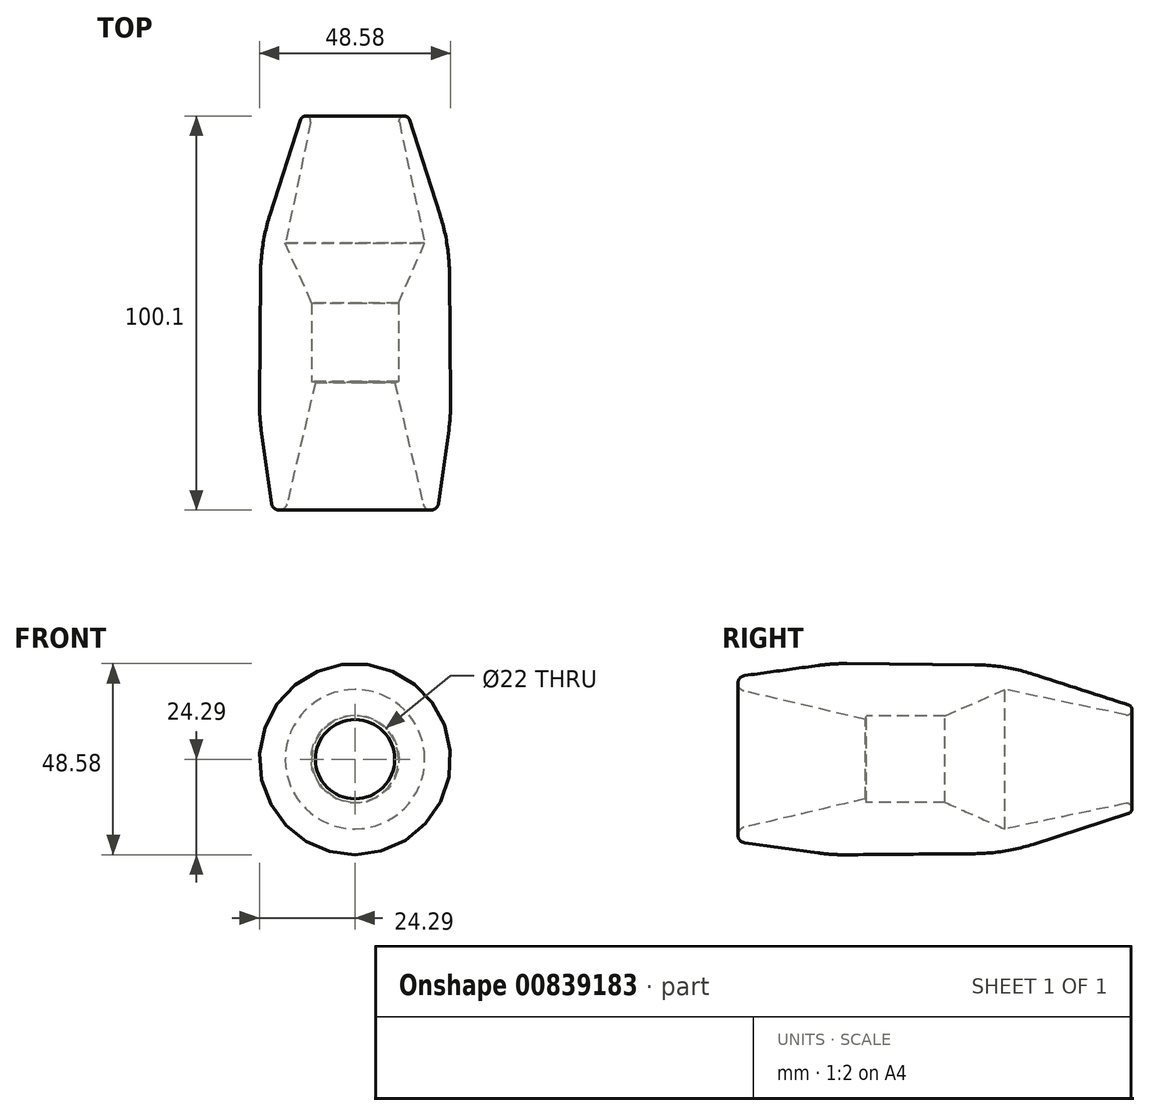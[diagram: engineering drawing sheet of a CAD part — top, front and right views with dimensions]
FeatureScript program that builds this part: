
annotation { "Feature Type Name" : "Feature", "Feature Type Description" : "" }
export const myFeature = defineFeature(function(context is Context, id is Id, definition is map)
    precondition{}
    {
        {
            var Q0;
            Q0=qCreatedBy(makeId("Right.planeOp"),FACE);
            var sketch = newSketch(context, id + "F0", { "sketchPlane" : qUnion([Q0])});
            skLineSegment(sketch, "E0", {"start": v(-43.22, -19.78) * mm, "end": v(-5.9, -11) * mm});
            skLineSegment(sketch, "E1", {"start": v(-5.9, -11) * mm, "end": v(18.33, -11) * mm});
            skLineSegment(sketch, "E2", {"start": v(18.33, -11) * mm, "end": v(33.48, -17.7) * mm});
            skLineSegment(sketch, "E3", {"start": v(-43.22, -19.78) * mm, "end": v(-10.31, -24.32) * mm});
            skLineSegment(sketch, "E4", {"start": v(33.48, -17.7) * mm, "end": v(65.5, -11) * mm});
            skLineSegment(sketch, "E5", {"start": v(65.5, -11) * mm, "end": v(66, -13.45) * mm});
            skLineSegment(sketch, "E6", {"start": v(66, -13.45) * mm, "end": v(33.48, -23.93) * mm});
            skLineSegment(sketch, "E7", {"start": v(33.48, -23.93) * mm, "end": v(-10.31, -24.32) * mm});
            skLineSegment(sketch, "E8", {"start": v(-41, 0) * mm, "end": v(54.87, 0) * mm, "construction": true});
            skLineSegment(sketch, "E9", {"start": v(-5.9, -11) * mm, "end": v(-1.9, -10.06) * mm});
            skLineSegment(sketch, "E10", {"start": v(-1.9, -10.06) * mm, "end": v(-1.68, -11) * mm});
            skLineSegment(sketch, "E11", {"start": v(-5.9, -11) * mm, "end": v(-5.9, 0) * mm});
            skLineSegment(sketch, "E12", {"start": v(-5.9, 0) * mm, "end": v(-22.9, 0) * mm});
            skLineSegment(sketch, "E13", {"start": v(-22.9, 0) * mm, "end": v(-22.9, -15) * mm});
            skSolve(sketch);
        }
        {
            var Q0;
            Q0=makeQuery(id+"F0.imprint","IMPRINT",FACE,{"disambiguationData":[TD([[makeQuery(id+"F0.imprint","IMPRINT",EDGE,{"derivedFrom":sQuery(id+"F0.wireOp",EDGE,"E0")}),-1.0]])]});
            var Q1;
            {var subQ0=sQuery(id+"F0.wireOp",EDGE,"E9");Q1=makeQuery(id+"F0.imprint","IMPRINT",FACE,{"disambiguationData":[TD([[makeQuery(id+"F0.imprint","IMPRINT",EDGE,{"derivedFrom":subQ0}),-1.0]])]});}
            var Q2;
            Q2=sQuery(id+"F0.wireOp",EDGE,"E8");
            revolve(context, id + "F1", {"surfaceOperationType" : NewSurfaceOperationType.NEW, "entities" : qUnion([Q0, Q1]), "axis" : qUnion([Q2]), "revolveType" : RevolveType.FULL});
        }
        {
            var Q0;
            Q0=makeQuery(id+"F1.opRevolve","SWEPT_EDGE",EDGE,{"disambiguationData":[OSD([sQuery(id+"F0.wireOp",EDGE,"E3"),sQuery(id+"F0.wireOp",EDGE,"E7")])]});
            var Q1;
            Q1=makeQuery(id+"F1.opRevolve","SWEPT_EDGE",EDGE,{"disambiguationData":[OSD([sQuery(id+"F0.wireOp",EDGE,"E6"),sQuery(id+"F0.wireOp",EDGE,"E7")])]});
            fillet(context, id + "F2", {"entities" : qUnion([Q0, Q1]), "radius" : 50 * mm, "tangentPropagation" : true, "allowEdgeOverflow" : false});
        }
        {
            var Q0;
            Q0=makeQuery(id+"F1.opRevolve","SWEPT_FACE",FACE,{"disambiguationData":[OSD([sQuery(id+"F0.wireOp",EDGE,"E5")])]});
            fillet(context, id + "F3", {"entities" : qUnion([Q0]), "radius" : (2.5 / 2) * mm, "tangentPropagation" : true, "allowEdgeOverflow" : false});
        }
        {
            var Q0;
            Q0=makeQuery(id+"F1.opRevolve","SWEPT_EDGE",EDGE,{"disambiguationData":[OSD([sQuery(id+"F0.wireOp",EDGE,"E0"),sQuery(id+"F0.wireOp",EDGE,"E3")])]});
            fillet(context, id + "F4", {"entities" : qUnion([Q0]), "radius" : 2 * mm, "tangentPropagation" : true, "allowEdgeOverflow" : false});
        }
    });
